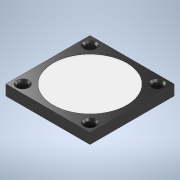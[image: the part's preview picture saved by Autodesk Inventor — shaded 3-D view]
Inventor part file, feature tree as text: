
AUTODESK INVENTOR PART (.ipt)
format: ipt  version: 2020 (Build 240168000, 168)  size: 138,240 bytes
history: native  units: mm
features: sketch x3, extrude x2, hole x1
ambient origin geometry x8: Origin, YZ Plane, XZ Plane, XY Plane, X Axis, Y Axis, Z Axis, Center Point
bodies: Solid1 (feature_tree)
feature tree (6):
  extrude  "Extrusion1"  Depth=40.0mm
  hole  "Hole1"  [1 undecoded]
  extrude  "Extrusion2"  Depth=0.1mm
  sketch  "Sketch1"  dims[d0=40.0mm d1=40.0mm]
  sketch  "Sketch2"  dims[d2=5.0mm d3=0.0mm d4=4.0mm]
  sketch  "Sketch3"  dims[d6=4.0mm d7=4.0mm d8=4.0mm d9=4.0mm d10=4.0mm d11=4.0mm d12=4.0mm d13=4.3mm d14=6.0mm d15=6.0mm d16=2.0mm d17=90.0deg d18=8.0mm d19=20.594885mm d21=20.0mm d22=20.0mm d23=35.0mm d24=0.1mm d25=0.0mm]
note: 1 required parameter value undecoded (feature->parameter linkage not recoverable at this tier; creation-order binding heuristic only, values carry confidence <= 0.55)
